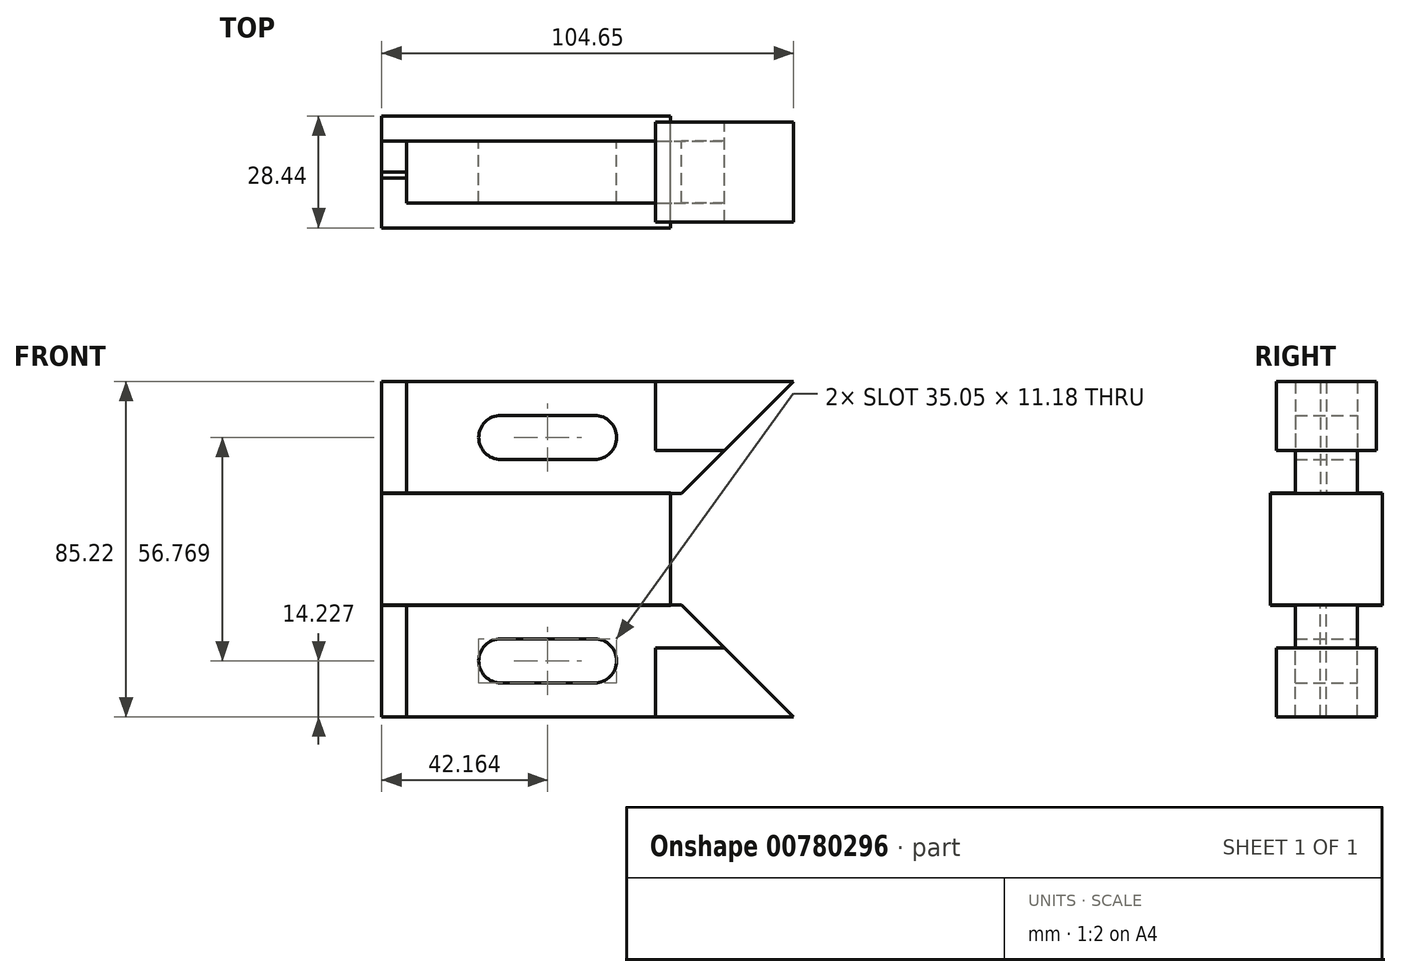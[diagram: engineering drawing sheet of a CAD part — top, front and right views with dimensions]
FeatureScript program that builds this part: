
annotation { "Feature Type Name" : "Feature", "Feature Type Description" : "" }
export const myFeature = defineFeature(function(context is Context, id is Id, definition is map)
    precondition{}
    {
        {
            var Q0;
            Q0=qCreatedBy(makeId("Front.planeOp"),FACE);
            var sketch = newSketch(context, id + "F0", { "sketchPlane" : qUnion([Q0])});
            skLineSegment(sketch, "E0.bottom", {"start": v(-61.94, 29.24) * mm, "end": v(42.7, 29.24) * mm});
            skLineSegment(sketch, "E0.top", {"start": v(-61.94, 0.8) * mm, "end": v(14.26, 0.8) * mm});
            skLineSegment(sketch, "E0.left", {"start": v(-61.94, 29.24) * mm, "end": v(-61.94, 0.8) * mm});
            skArc(sketch, "E1", {"start": v(-31.71, 20.6) * mm, "mid": v(-37.3, 15.02) * mm, "end": v(-31.71, 9.43) * mm});
            skArc(sketch, "E2", {"start": v(-7.84, 9.43) * mm, "mid": v(-2.25, 15.02) * mm, "end": v(-7.84, 20.6) * mm});
            skLineSegment(sketch, "E3", {"start": v(-55.6, 29.24) * mm, "end": v(-55.6, 0.8) * mm});
            skLineSegment(sketch, "E4", {"start": v(-31.71, 20.6) * mm, "end": v(-7.84, 20.6) * mm});
            skLineSegment(sketch, "E5", {"start": v(-31.71, 9.43) * mm, "end": v(-7.84, 9.43) * mm});
            skLineSegment(sketch, "E6", {"start": v(7.66, 29.24) * mm, "end": v(7.66, 11.71) * mm});
            skLineSegment(sketch, "E7", {"start": v(42.7, 29.24) * mm, "end": v(14.26, 0.8) * mm});
            skLineSegment(sketch, "E8", {"start": v(7.66, 11.71) * mm, "end": v(25.18, 11.71) * mm});
            skLineSegment(sketch, "E9.bottom", {"start": v(-61.94, 0.8) * mm, "end": v(11.47, 0.8) * mm});
            skLineSegment(sketch, "E9.top", {"start": v(-61.94, -27.66) * mm, "end": v(11.47, -27.66) * mm});
            skLineSegment(sketch, "E9.left", {"start": v(-61.94, 0.8) * mm, "end": v(-61.94, -27.66) * mm});
            skLineSegment(sketch, "E9.right", {"start": v(11.47, 0.8) * mm, "end": v(11.47, -27.66) * mm});
            skSolve(sketch);
        }
        {
            var Q0;
            {var subQ0=sQuery(id+"F0.wireOp",EDGE,"E6");Q0=makeQuery(id+"F0.imprint","IMPRINT",FACE,{"disambiguationData":[TD([[makeQuery(id+"F0.imprint","IMPRINT",EDGE,{"derivedFrom":subQ0}),1.0]])]});}
            extrude(context, id + "F1", {"entities" : qUnion([Q0]), "endBound" : BoundingType.SYMMETRIC, "depth" : 25.4 * mm, "offsetDistance" : 25.4 * mm});
        }
        {
            var Q0;
            Q0=makeQuery(id+"F0.imprint","IMPRINT",FACE,{"disambiguationData":[TD([[makeQuery(id+"F0.imprint","IMPRINT",EDGE,{"derivedFrom":sQuery(id+"F0.wireOp",EDGE,"E9.top")}),1.0]])]});
            extrude(context, id + "F2", {"entities" : qUnion([Q0]), "endBound" : BoundingType.SYMMETRIC, "depth" : 28.45 * mm, "offsetDistance" : 25.4 * mm});
        }
        {
            var Q0;
            Q0=makeQuery(id+"F0.imprint","IMPRINT",FACE,{"disambiguationData":[TD([[makeQuery(id+"F0.imprint","IMPRINT",EDGE,{"derivedFrom":sQuery(id+"F0.wireOp",EDGE,"E1")}),-1.0]])]});
            extrude(context, id + "F3", {"entities" : qUnion([Q0]), "endBound" : BoundingType.SYMMETRIC, "depth" : 15.75 * mm, "offsetDistance" : 25.4 * mm});
        }
        {
            var Q0;
            {var subQ2=sQuery(id+"F0.wireOp",EDGE,"E0.left");Q0=makeQuery(id+"F0.imprint","IMPRINT",FACE,{"disambiguationData":[TD([[makeQuery(id+"F0.imprint","IMPRINT",EDGE,{"derivedFrom":subQ2}),1.0]])]});}
            extrude(context, id + "F4", {"entities" : qUnion([Q0]), "oppositeDirection" : true, "depth" : 7.87 * mm, "offsetDistance" : 25.4 * mm});
        }
        {
            var Q0;
            {var subQ2=sQuery(id+"F0.wireOp",EDGE,"E0.left");Q0=makeQuery(id+"F0.imprint","IMPRINT",FACE,{"disambiguationData":[TD([[makeQuery(id+"F0.imprint","IMPRINT",EDGE,{"derivedFrom":subQ2}),1.0]])]});}
            extrude(context, id + "F5", {"entities" : qUnion([Q0]), "depth" : 1.52 * mm, "offsetDistance" : 25.4 * mm});
        }
        {
            var Q0;
            Q0=makeQuery(id+"F2.opExtrude","SWEPT_FACE",FACE,{"disambiguationData":[OSD([sQuery(id+"F0.wireOp",EDGE,"E9.top")])]});
            cPlane(context, id + "F6", {"entities" : qUnion([Q0]), "cplaneType" : CPlaneType.OFFSET, "offset" : 14.29 * mm, "oppositeDirection" : true, "width" : 152.4 * mm, "height" : 152.4 * mm});
        }
        {
            var Q0;
            Q0=makeQuery(id+"F3.opExtrude","SWEPT_BODY",BODY,{"disambiguationData":[OSD([sQuery(id+"F0.wireOp",EDGE,"E0.bottom"),sQuery(id+"F0.wireOp",EDGE,"E0.top"),sQuery(id+"F0.wireOp",EDGE,"E1"),sQuery(id+"F0.wireOp",EDGE,"E2"),sQuery(id+"F0.wireOp",EDGE,"E3"),sQuery(id+"F0.wireOp",EDGE,"E4"),sQuery(id+"F0.wireOp",EDGE,"E5"),sQuery(id+"F0.wireOp",EDGE,"E6"),sQuery(id+"F0.wireOp",EDGE,"E7"),sQuery(id+"F0.wireOp",EDGE,"E8")])]});
            var Q1;
            Q1=makeQuery(id+"F4.opExtrude","SWEPT_BODY",BODY,{"disambiguationData":[OSD([sQuery(id+"F0.wireOp",EDGE,"E0.bottom"),sQuery(id+"F0.wireOp",EDGE,"E0.top"),sQuery(id+"F0.wireOp",EDGE,"E0.left"),sQuery(id+"F0.wireOp",EDGE,"E3")])]});
            var Q2;
            Q2=makeQuery(id+"F5.opExtrude","SWEPT_BODY",BODY,{"disambiguationData":[OSD([sQuery(id+"F0.wireOp",EDGE,"E0.bottom"),sQuery(id+"F0.wireOp",EDGE,"E0.top"),sQuery(id+"F0.wireOp",EDGE,"E0.left"),sQuery(id+"F0.wireOp",EDGE,"E3")])]});
            var Q3;
            Q3=makeQuery(id+"F2.opExtrude","SWEPT_BODY",BODY,{"disambiguationData":[OSD([sQuery(id+"F0.wireOp",EDGE,"E0.top"),sQuery(id+"F0.wireOp",EDGE,"E9.top"),sQuery(id+"F0.wireOp",EDGE,"E9.left"),sQuery(id+"F0.wireOp",EDGE,"E9.right")])]});
            var Q4;
            Q4=makeQuery(id+"F1.opExtrude","SWEPT_BODY",BODY,{"disambiguationData":[OSD([sQuery(id+"F0.wireOp",EDGE,"E0.bottom"),sQuery(id+"F0.wireOp",EDGE,"E6"),sQuery(id+"F0.wireOp",EDGE,"E7"),sQuery(id+"F0.wireOp",EDGE,"E8")])]});
            var Q5;
            Q5=qCreatedBy(id+"F6.planeOp",FACE);
            mirror(context, id + "F7", {"entities" : qUnion([Q0, Q1, Q2, Q3, Q4]), "mirrorPlane" : qUnion([Q5])});
        }
    });
